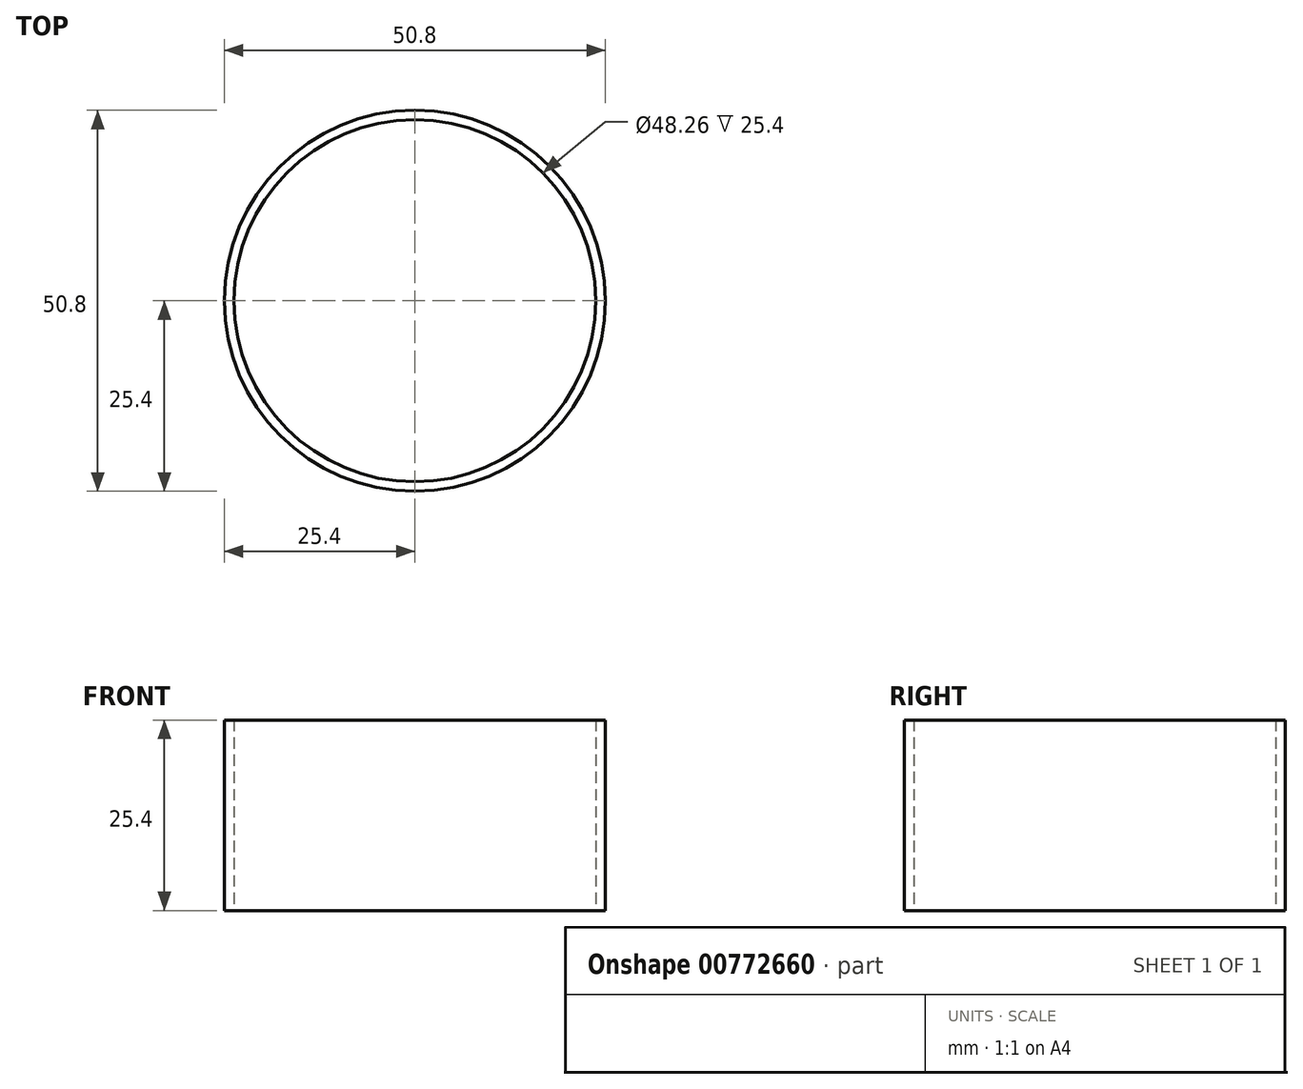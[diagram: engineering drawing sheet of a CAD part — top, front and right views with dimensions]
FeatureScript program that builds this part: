
annotation { "Feature Type Name" : "Feature", "Feature Type Description" : "" }
export const myFeature = defineFeature(function(context is Context, id is Id, definition is map)
    precondition{}
    {
        {
            var Q0;
            Q0=qCreatedBy(makeId("Top.planeOp"),FACE);
            var sketch = newSketch(context, id + "F0", { "sketchPlane" : qUnion([Q0])});
            skCircle(sketch, "E0", {"center": v(0, 0) * mm, "radius": 25.4 * mm});
            skCircle(sketch, "E1", {"center": v(0, 0) * mm, "radius": 24.13 * mm});
            skSolve(sketch);
        }
        {
            var Q0;
            Q0=makeQuery(id+"F0.imprint","IMPRINT",FACE,{"disambiguationData":[TD([[makeQuery(id+"F0.imprint","IMPRINT",EDGE,{"derivedFrom":sQuery(id+"F0.wireOp",EDGE,"E0")}),1.0]])]});
            extrude(context, id + "F1", {"entities" : qUnion([Q0]), "depth" : 25.4 * mm, "offsetDistance" : 25.4 * mm});
        }
    });
